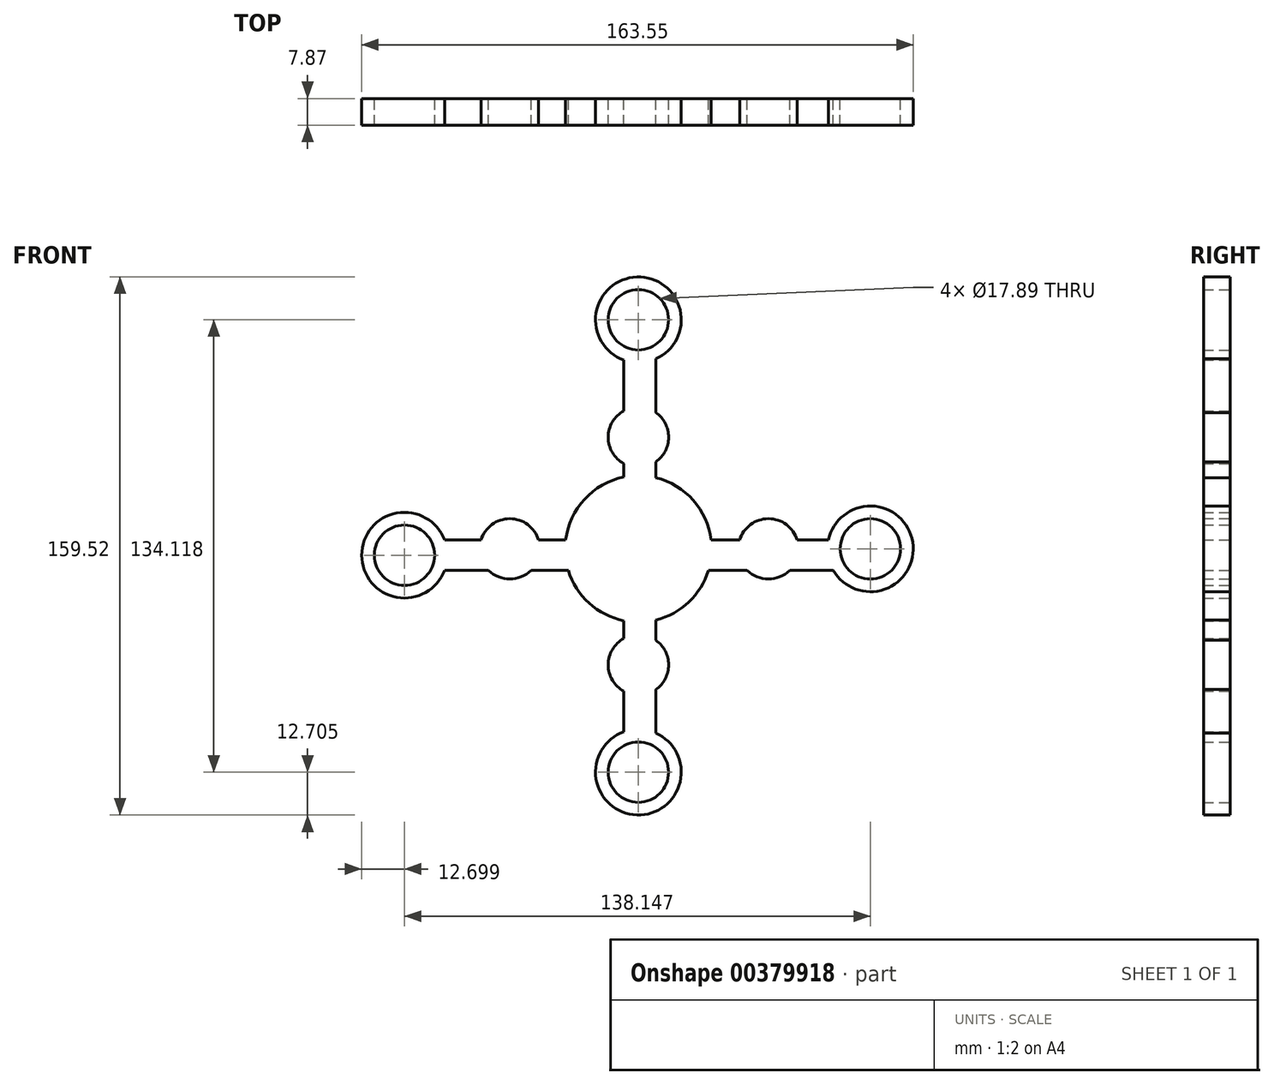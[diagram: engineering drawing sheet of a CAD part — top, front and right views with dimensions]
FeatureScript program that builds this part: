
annotation { "Feature Type Name" : "Feature", "Feature Type Description" : "" }
export const myFeature = defineFeature(function(context is Context, id is Id, definition is map)
    precondition{}
    {
        {
            var Q0;
            Q0=qCreatedBy(makeId("Front.planeOp"),FACE);
            var sketch = newSketch(context, id + "F0", { "sketchPlane" : qUnion([Q0])});
            skLineSegment(sketch, "E0.bottom", {"start": v(-4.32, 0) * mm, "end": v(5.18, 0) * mm});
            skLineSegment(sketch, "E0.top", {"start": v(-4.32, 70.51) * mm, "end": v(5.18, 70.51) * mm});
            skLineSegment(sketch, "E0.left", {"start": v(-4.32, 0) * mm, "end": v(-4.32, 70.51) * mm});
            skLineSegment(sketch, "E0.right", {"start": v(5.18, 0) * mm, "end": v(5.18, 70.51) * mm});
            skLineSegment(sketch, "E1.top", {"start": v(-4.32, -68.79) * mm, "end": v(5.18, -68.79) * mm});
            skLineSegment(sketch, "E1.left", {"start": v(-4.32, 0) * mm, "end": v(-4.32, -68.79) * mm});
            skLineSegment(sketch, "E1.right", {"start": v(5.18, 0) * mm, "end": v(5.18, -68.79) * mm});
            skLineSegment(sketch, "E2.bottom", {"start": v(5.18, 0) * mm, "end": v(5.18, 0) * mm});
            skLineSegment(sketch, "E2.top", {"start": v(5.18, 2.6) * mm, "end": v(5.18, 2.6) * mm});
            skLineSegment(sketch, "E2.left", {"start": v(5.18, 0) * mm, "end": v(5.18, 2.6) * mm});
            skLineSegment(sketch, "E2.right", {"start": v(5.18, 0) * mm, "end": v(5.18, 2.6) * mm});
            skLineSegment(sketch, "E3.bottom", {"start": v(5.18, 2.6) * mm, "end": v(73.4, 2.6) * mm});
            skLineSegment(sketch, "E3.top", {"start": v(5.18, -6.33) * mm, "end": v(73.4, -6.33) * mm});
            skLineSegment(sketch, "E3.left", {"start": v(5.18, 2.6) * mm, "end": v(5.18, -6.33) * mm});
            skLineSegment(sketch, "E3.right", {"start": v(73.4, 2.6) * mm, "end": v(73.4, -6.33) * mm});
            skLineSegment(sketch, "E4.bottom", {"start": v(-4.32, -6.33) * mm, "end": v(-71.95, -6.33) * mm});
            skLineSegment(sketch, "E4.top", {"start": v(-4.32, 2.6) * mm, "end": v(-71.95, 2.6) * mm});
            skLineSegment(sketch, "E4.left", {"start": v(-4.32, -6.33) * mm, "end": v(-4.32, 2.6) * mm});
            skLineSegment(sketch, "E4.right", {"start": v(-71.95, -6.33) * mm, "end": v(-71.95, 2.6) * mm});
            skCircle(sketch, "E5", {"center": v(0, 67.92) * mm, "radius": 12.7 * mm});
            skCircle(sketch, "E6", {"center": v(-69.36, -1.87) * mm, "radius": 12.7 * mm});
            skPoint(sketch, "E6.centerSnap0", {"position": v(-71.95, -1.87) * mm});
            skCircle(sketch, "E7", {"center": v(0, -66.2) * mm, "radius": 12.7 * mm});
            skCircle(sketch, "E8", {"center": v(68.79, 0) * mm, "radius": 12.7 * mm});
            skCircle(sketch, "E9", {"center": v(-69.36, -1.87) * mm, "radius": 8.95 * mm});
            skCircle(sketch, "E10", {"center": v(0, -66.2) * mm, "radius": 8.95 * mm});
            skCircle(sketch, "E11", {"center": v(68.79, 0) * mm, "radius": 8.95 * mm});
            skCircle(sketch, "E12", {"center": v(0, 67.92) * mm, "radius": 8.95 * mm});
            skCircle(sketch, "E13", {"center": v(0, 33.1) * mm, "radius": 8.95 * mm});
            skCircle(sketch, "E14", {"center": v(-38.13, 0) * mm, "radius": 8.95 * mm});
            skPoint(sketch, "E14.centerSnap0", {"position": v(-38.13, 2.6) * mm});
            skCircle(sketch, "E15", {"center": v(0, -34.4) * mm, "radius": 8.95 * mm});
            skPoint(sketch, "E15.centerSnap0", {"position": v(5.18, -34.4) * mm});
            skCircle(sketch, "E16", {"center": v(38.57, 0) * mm, "radius": 8.95 * mm});
            skCircle(sketch, "E17", {"center": v(0, 0) * mm, "radius": 21.73 * mm});
            skSolve(sketch);
        }
        {
            var Q0;
            Q0 = qSketchRegion(id + "F0", true);
            extrude(context, id + "F1", {"entities" : qUnion([Q0]), "depth" : 7.87 * mm});
        }
    });
